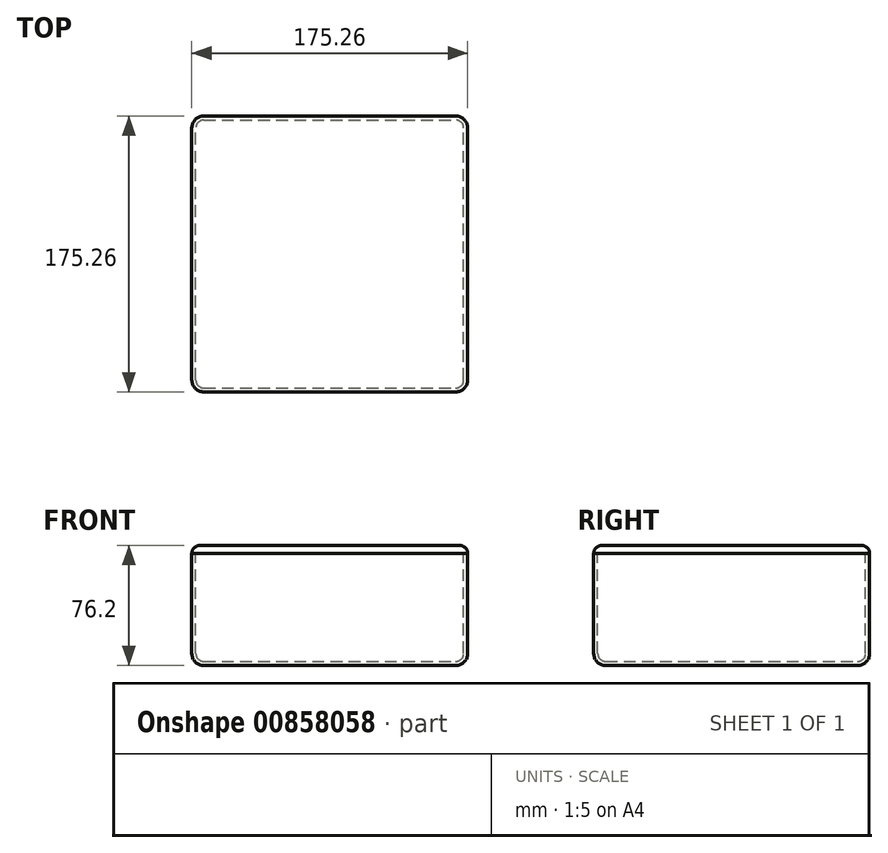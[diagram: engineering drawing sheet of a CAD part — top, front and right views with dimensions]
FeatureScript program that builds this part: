
annotation { "Feature Type Name" : "Feature", "Feature Type Description" : "" }
export const myFeature = defineFeature(function(context is Context, id is Id, definition is map)
    precondition{}
    {
        {
            var Q0;
            Q0=qCreatedBy(makeId("Top.planeOp"),FACE);
            var sketch = newSketch(context, id + "F0", { "sketchPlane" : qUnion([Q0])});
            skLineSegment(sketch, "E0.bottom", {"start": v(-87.63, -87.63) * mm, "end": v(87.63, -87.63) * mm});
            skLineSegment(sketch, "E0.top", {"start": v(-87.63, 87.63) * mm, "end": v(87.63, 87.63) * mm});
            skLineSegment(sketch, "E0.left", {"start": v(-87.63, -87.63) * mm, "end": v(-87.63, 87.63) * mm});
            skLineSegment(sketch, "E0.right", {"start": v(87.63, -87.63) * mm, "end": v(87.63, 87.63) * mm});
            skPoint(sketch, "E0.middle", {"position": v(0, 0) * mm});
            skSolve(sketch);
        }
        {
            var Q0;
            Q0=makeQuery(id+"F0.imprint","IMPRINT",FACE,{"disambiguationData":[TD([[makeQuery(id+"F0.imprint","IMPRINT",EDGE,{"derivedFrom":sQuery(id+"F0.wireOp",EDGE,"E0.bottom")}),1.0]])]});
            extrude(context, id + "F1", {"entities" : qUnion([Q0]), "depth" : 71.12 * mm, "offsetDistance" : 25.4 * mm});
        }
        {
            var Q0;
            Q0=makeQuery(id+"F1.opExtrude","SWEPT_EDGE",EDGE,{"disambiguationData":[OSD([sQuery(id+"F0.wireOp",EDGE,"E0.top"),sQuery(id+"F0.wireOp",EDGE,"E0.left")])]});
            var Q1;
            Q1=makeQuery(id+"F1.opExtrude","SWEPT_EDGE",EDGE,{"disambiguationData":[OSD([sQuery(id+"F0.wireOp",EDGE,"E0.top"),sQuery(id+"F0.wireOp",EDGE,"E0.right")])]});
            var Q2;
            Q2=makeQuery(id+"F1.opExtrude","SWEPT_EDGE",EDGE,{"disambiguationData":[OSD([sQuery(id+"F0.wireOp",EDGE,"E0.bottom"),sQuery(id+"F0.wireOp",EDGE,"E0.left")])]});
            var Q3;
            Q3=makeQuery(id+"F1.opExtrude","SWEPT_EDGE",EDGE,{"disambiguationData":[OSD([sQuery(id+"F0.wireOp",EDGE,"E0.bottom"),sQuery(id+"F0.wireOp",EDGE,"E0.right")])]});
            var Q4;
            Q4=makeQuery(id+"F1.opExtrude","CAP_EDGE",EDGE,{"disambiguationData":[OSD([sQuery(id+"F0.wireOp",EDGE,"E0.left")])],"isStart":true});
            var Q5;
            Q5=makeQuery(id+"F1.opExtrude","CAP_EDGE",EDGE,{"disambiguationData":[OSD([sQuery(id+"F0.wireOp",EDGE,"E0.bottom")])],"isStart":true});
            var Q6;
            Q6=makeQuery(id+"F1.opExtrude","CAP_EDGE",EDGE,{"disambiguationData":[OSD([sQuery(id+"F0.wireOp",EDGE,"E0.top")])],"isStart":true});
            var Q7;
            Q7=makeQuery(id+"F1.opExtrude","CAP_EDGE",EDGE,{"disambiguationData":[OSD([sQuery(id+"F0.wireOp",EDGE,"E0.right")])],"isStart":true});
            fillet(context, id + "F2", {"entities" : qUnion([Q0, Q1, Q2, Q3, Q4, Q5, Q6, Q7]), "radius" : 7.62 * mm, "tangentPropagation" : true, "allowEdgeOverflow" : false});
        }
        {
            var Q0;
            Q0=makeQuery(id+"F1.opExtrude","CAP_FACE",FACE,{"disambiguationData":[OSD([sQuery(id+"F0.wireOp",EDGE,"E0.bottom"),sQuery(id+"F0.wireOp",EDGE,"E0.top"),sQuery(id+"F0.wireOp",EDGE,"E0.left"),sQuery(id+"F0.wireOp",EDGE,"E0.right")])],"isStart":false});
            shell(context, id + "F3", {"entities" : qUnion([Q0]), "thickness" : 2.54 * mm});
        }
        {
            var Q0;
            Q0=makeQuery(id+"F1.opExtrude","CAP_FACE",FACE,{"disambiguationData":[OSD([sQuery(id+"F0.wireOp",EDGE,"E0.bottom"),sQuery(id+"F0.wireOp",EDGE,"E0.top"),sQuery(id+"F0.wireOp",EDGE,"E0.left"),sQuery(id+"F0.wireOp",EDGE,"E0.right")])],"isStart":false});
            var sketch = newSketch(context, id + "F4", { "sketchPlane" : qUnion([Q0])});
            skArc(sketch, "E1.0", {"start": v(-80.01, 87.63) * mm, "mid": v(-85.4, 85.4) * mm, "end": v(-87.63, 80.01) * mm});
            skLineSegment(sketch, "E1.1", {"start": v(-87.63, -80.01) * mm, "end": v(-87.63, 80.01) * mm});
            skArc(sketch, "E1.2", {"start": v(-87.63, -80.01) * mm, "mid": v(-85.4, -85.4) * mm, "end": v(-80, -87.63) * mm});
            skLineSegment(sketch, "E1.3", {"start": v(-80, -87.63) * mm, "end": v(80.01, -87.63) * mm});
            skArc(sketch, "E1.4", {"start": v(80.01, -87.63) * mm, "mid": v(85.4, -85.4) * mm, "end": v(87.63, -80) * mm});
            skLineSegment(sketch, "E1.5", {"start": v(87.63, -80) * mm, "end": v(87.63, 80.01) * mm});
            skArc(sketch, "E1.6", {"start": v(87.63, 80.01) * mm, "mid": v(85.4, 85.4) * mm, "end": v(80, 87.63) * mm});
            skLineSegment(sketch, "E1.7", {"start": v(-80.01, 87.63) * mm, "end": v(80, 87.63) * mm});
            skSolve(sketch);
        }
        {
            var Q0;
            Q0 = qSketchRegion(id + "F4", true);
            extrude(context, id + "F5", {"entities" : qUnion([Q0]), "depth" : 5.08 * mm, "offsetDistance" : 25.4 * mm});
        }
        {
            var Q0;
            Q0=makeQuery(id+"F5.opExtrude","CAP_EDGE",EDGE,{"disambiguationData":[OSD([sQuery(id+"F4.wireOp",EDGE,"E1.5")])],"isStart":false});
            fillet(context, id + "F6", {"entities" : qUnion([Q0]), "radius" : 5.08 * mm, "tangentPropagation" : true, "allowEdgeOverflow" : false});
        }
    });
